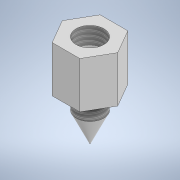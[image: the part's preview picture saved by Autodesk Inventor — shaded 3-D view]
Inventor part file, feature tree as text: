
AUTODESK INVENTOR PART (.ipt)
format: ipt  version: 2020 (Build 240168000, 168)  size: 128,512 bytes
history: native  units: in
note: dims shown in document units (in); Inventor stores cm internally (conversion verified against a paired STEP export)
features: extrude x4, sketch x4, thread x2
ambient origin geometry x8: Origin, YZ Plane, XZ Plane, XY Plane, X Axis, Y Axis, Z Axis, Center Point
bodies: Solid1 (feature_tree)
feature tree (10):
  extrude  "Extrusion1"  Depth=0.1969in TaperAngle=0.0deg
  extrude  "Extrusion2"  Depth=0.5906in
  thread  "Thread1"  [1 undecoded]
  extrude  "Extrusion3"  Depth=0.1181in
  extrude  "Extrusion4"  Depth=0.1969in
  thread  "Thread2"  [1 undecoded]
  sketch  "Sketch1"  dims[d0=0.1181in d1=0.1969in d2=0.0in]
  sketch  "Sketch2"  dims[d3=0.0039in d4=0.5906in d5=0.1718in d6=0.4681in d7=0.0in]
  sketch  "Sketch3"  dims[d8=0.1181in d9=0.1181in]
  sketch  "Sketch4"  dims[d10=60.0deg d11=0.1181in d12=0.1969in d13=0.0in d14=0.1969in d15=0.0in d16=0.074in d17=0.0in d18=0.5in d19=0.0344in d20=0.5in d21=0.0344in]
note: 2 required parameter values undecoded (feature->parameter linkage not recoverable at this tier; creation-order binding heuristic only, values carry confidence <= 0.55)
